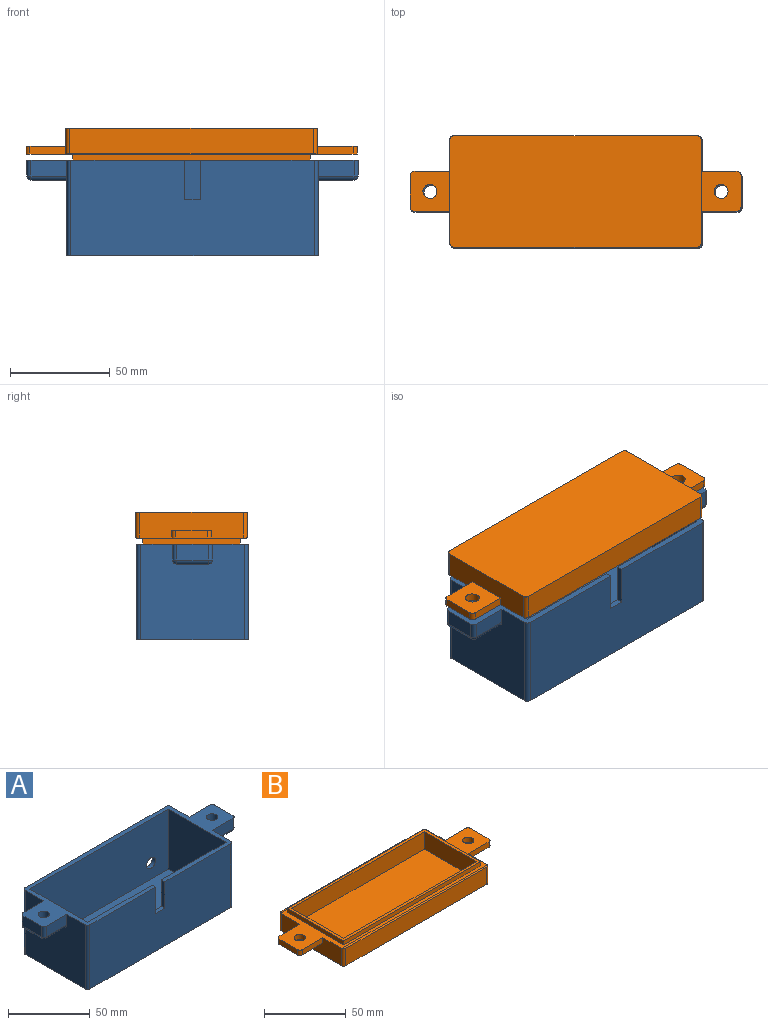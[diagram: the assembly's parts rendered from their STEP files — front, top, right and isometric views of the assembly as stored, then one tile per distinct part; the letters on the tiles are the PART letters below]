
ASSEMBLY  parts=2 mates=1
PART A: 49 faces, bbox 166x56x48 mm
  f0: plane 120x45mm, normal (0,-1,0), area 5232.7mm2, adj f2,f5,f8,f12,f44,f45,f46,f47
  f1: plane 122x48mm, normal (0,1,0), area 5688.7mm2, adj f2,f9,f29,f30,f44,f45,f46,f47
  f2: plane 166x56mm, normal (0,0,1), area 1748.2mm2, adj f0,f1,f3,f4,f5,f6,f7,f8
  f3: plane 122x48mm, normal (0,-1,0), area 5696mm2, adj f2,f9,f31,f32,f41,f42,f43
  f4: plane 52x48mm, normal (-1,0,0), area 2297.7mm2, adj f2,f9,f13,f14,f17,f23,f25,f30
  f5: plane 50x45mm, normal (-1,0,0), area 2250mm2, adj f0,f2,f6,f12
  f6: plane 120x45mm, normal (0,1,0), area 5240mm2, adj f2,f5,f8,f12,f41,f42,f43
  f7: plane 52x48mm, normal (1,0,0), area 2297.7mm2, adj f2,f9,f18,f19,f22,f26,f27,f29
  f8: plane 50x45mm, normal (1,0,0), area 2250mm2, adj f0,f2,f6,f12
  f9: plane 126x56mm, normal (0,0,-1), area 6975.6mm2, adj f1,f3,f4,f7,f10,f11,f29,f30
  f10: cylinder r=3.5mm len=7mm, axis (0,0,-1), area 66mm2, adj f9,f12
  f11: cylinder r=3.5mm len=7mm, axis (0,0,-1), area 66mm2, adj f9,f12
  f12: plane 120x50mm, normal (0,0,1), area 5923mm2, adj f0,f5,f6,f8,f10,f11
  f13: plane 18x8mm, normal (0,-1,0), area 144mm2, adj f2,f4,f23,f37
  f14: plane 18x8mm, normal (0,1,0), area 144mm2, adj f2,f4,f25,f39
  f15: plane 16x8mm, normal (-1,0,0), area 128mm2, adj f2,f24,f37,f39
  f16: cylinder r=3.5mm len=10mm, axis (0,0,1), area 219.9mm2, adj f2,f17
  f17: plane 18x16mm, normal (0,0,-1), area 249.5mm2, adj f4,f16,f23,f24,f25
  f18: plane 18x8mm, normal (0,1,0), area 144mm2, adj f2,f7,f26,f33
  f19: plane 18x8mm, normal (0,-1,0), area 144mm2, adj f2,f7,f27,f35
  f20: plane 16x8mm, normal (1,0,0), area 128mm2, adj f2,f28,f33,f35
  f21: cylinder r=3.5mm len=10mm, axis (0,0,1), area 219.9mm2, adj f2,f22
  f22: plane 18x16mm, normal (0,0,-1), area 249.5mm2, adj f7,f21,f26,f27,f28
  f23: cylinder r=2mm len=18mm, axis (-1,0,0), area 56.5mm2, adj f4,f13,f17,f38
  f24: cylinder r=2mm len=16mm, axis (0,1,0), area 50.3mm2, adj f15,f17,f38,f40
  f25: cylinder r=2mm len=18mm, axis (1,0,0), area 56.5mm2, adj f4,f14,f17,f40
  f26: cylinder r=2mm len=18mm, axis (1,0,0), area 56.5mm2, adj f7,f18,f22,f34
  f27: cylinder r=2mm len=18mm, axis (-1,0,0), area 56.5mm2, adj f7,f19,f22,f36
  f28: cylinder r=2mm len=16mm, axis (0,-1,0), area 50.3mm2, adj f20,f22,f34,f36
  f29: cylinder r=2mm len=48mm, axis (0,0,1), area 150.8mm2, adj f1,f2,f7,f9
  f30: cylinder r=2mm len=48mm, axis (0,0,-1), area 150.8mm2, adj f1,f2,f4,f9
  f31: cylinder r=2mm len=48mm, axis (0,0,1), area 150.8mm2, adj f2,f3,f4,f9
  f32: cylinder r=2mm len=48mm, axis (0,0,-1), area 150.8mm2, adj f2,f3,f7,f9
  f33: cylinder r=2mm len=8mm, axis (0,0,1), area 25.1mm2, adj f2,f18,f20,f34
  f34: sphere r=2mm, area 6.3mm2, adj f26,f28,f33
  f35: cylinder r=2mm len=8mm, axis (0,0,-1), area 25.1mm2, adj f2,f19,f20,f36
  f36: sphere r=2mm, area 6.3mm2, adj f27,f28,f35
  f37: cylinder r=2mm len=8mm, axis (0,0,1), area 25.1mm2, adj f2,f13,f15,f38
  f38: sphere r=2mm, area 6.3mm2, adj f23,f24,f37
  f39: cylinder r=2mm len=8mm, axis (0,0,-1), area 25.1mm2, adj f2,f14,f15,f40
  f40: sphere r=2mm, area 6.3mm2, adj f24,f25,f39
  f41: plane 20x3mm, normal (-1,0,0), area 60mm2, adj f2,f3,f6,f42
  f42: plane 8x3mm, normal (0,0,1), area 24mm2, adj f3,f6,f41,f43
  f43: plane 20x3mm, normal (1,0,0), area 60mm2, adj f2,f3,f6,f42
  f44: plane 9x3mm, normal (1,0,0), area 27mm2, adj f0,f1,f45,f47
  f45: plane 13x3mm, normal (0,0,1), area 39mm2, adj f0,f1,f44,f46
  f46: plane 9x3mm, normal (-1,0,0), area 27mm2, adj f0,f1,f45,f47
  f47: plane 13x3mm, normal (0,0,-1), area 39mm2, adj f0,f1,f44,f46
  f48: cylinder r=4mm len=8mm, axis (0,-1,0), area 75.4mm2, adj f0,f1
PART B: 36 faces, bbox 166x56x16 mm
  f0: plane 52x13mm, normal (1,0,0), area 596mm2, adj f6,f15,f17,f23,f26,f27,f35
  f1: plane 45x13mm, normal (-1,0,0), area 585mm2, adj f2,f4,f5,f34
  f2: plane 115x13mm, normal (0,-1,0), area 1495mm2, adj f1,f3,f5,f34
  f3: plane 45x13mm, normal (1,0,0), area 585mm2, adj f2,f4,f5,f34
  f4: plane 115x13mm, normal (0,1,0), area 1495mm2, adj f1,f3,f5,f34
  f5: plane 119x49mm, normal (0,0,1), area 656mm2, adj f1,f2,f3,f4,f8,f9,f10,f11
  f6: plane 20x20mm, normal (0,0,-1), area 359.8mm2, adj f0,f15,f16,f17,f22,f31,f32
  f7: cylinder r=8mm len=125.87mm, axis (1,0,0), area 188.4mm2, adj f14,f23,f25,f26
  f8: plane 49x3mm, normal (1,0,0), area 147mm2, adj f5,f9,f11,f23
  f9: plane 119x3mm, normal (0,1,0), area 357mm2, adj f5,f8,f10,f23
  f10: plane 49x3mm, normal (-1,0,0), area 147mm2, adj f5,f9,f11,f23
  f11: plane 119x3mm, normal (0,-1,0), area 357mm2, adj f5,f8,f10,f23
  f12: plane 18x4mm, normal (0,-1,0), area 72mm2, adj f13,f23,f24,f30
  f13: plane 52x13mm, normal (-1,0,0), area 596mm2, adj f12,f19,f23,f24,f25,f28,f35
  f14: plane 122x12.86mm, normal (0,-1,0), area 1568.7mm2, adj f7,f25,f26,f35
  f15: plane 18x4mm, normal (0,-1,0), area 72mm2, adj f0,f6,f23,f31
  f16: plane 16x4mm, normal (1,0,0), area 64mm2, adj f6,f23,f31,f32
  f17: plane 18x4mm, normal (0,1,0), area 72mm2, adj f0,f6,f23,f32
  f18: plane 122x12.86mm, normal (0,1,0), area 1568.7mm2, adj f27,f28,f33,f35
  f19: plane 18x4mm, normal (0,1,0), area 72mm2, adj f13,f23,f24,f29
  f20: cylinder r=3.5mm len=7mm, axis (0,0,-1), area 88mm2, adj f23,f24
  f21: plane 16x4mm, normal (-1,0,0), area 64mm2, adj f23,f24,f29,f30
  f22: cylinder r=3.5mm len=7mm, axis (0,0,-1), area 88mm2, adj f6,f23
  f23: plane 166x53mm, normal (0,0,1), area 1566.6mm2, adj f0,f7,f8,f9,f10,f11,f12,f13
  f24: plane 20x20mm, normal (0,0,-1), area 359.8mm2, adj f12,f13,f19,f20,f21,f29,f30
  f25: cylinder r=2mm len=13mm, axis (0,0,1), area 40.7mm2, adj f7,f13,f14,f23,f35
  f26: cylinder r=2mm len=13mm, axis (0,0,-1), area 40.7mm2, adj f0,f7,f14,f23,f35
  f27: cylinder r=2mm len=13mm, axis (0,0,1), area 40.7mm2, adj f0,f18,f23,f33,f35
  f28: cylinder r=2mm len=13mm, axis (0,0,-1), area 40.7mm2, adj f13,f18,f23,f33,f35
  f29: cylinder r=2mm len=4mm, axis (0,0,-1), area 12.6mm2, adj f19,f21,f23,f24
  f30: cylinder r=2mm len=4mm, axis (0,0,1), area 12.6mm2, adj f12,f21,f23,f24
  f31: cylinder r=2mm len=4mm, axis (0,0,1), area 12.6mm2, adj f6,f15,f16,f23
  f32: cylinder r=2mm len=4mm, axis (0,0,-1), area 12.6mm2, adj f6,f16,f17,f23
  f33: cylinder r=8mm len=125.87mm, axis (-1,0,0), area 188.4mm2, adj f18,f23,f27,f28
  f34: plane 115x45mm, normal (0,0,1), area 5175mm2, adj f1,f2,f3,f4
  f35: plane 126x56mm, normal (0,0,-1), area 7052.6mm2, adj f0,f13,f14,f18,f25,f26,f27,f28
PLACE A t=(-22.64,-7.95,-16.31)mm fixed
PLACE B rot(axis=(1,0,0),180deg) t=(-23.14,-7.45,38.69)mm
MATE slider B.f5 <-> A.f2  axis (0,0,-1) through (-82.64,17.05,31.69)mm
